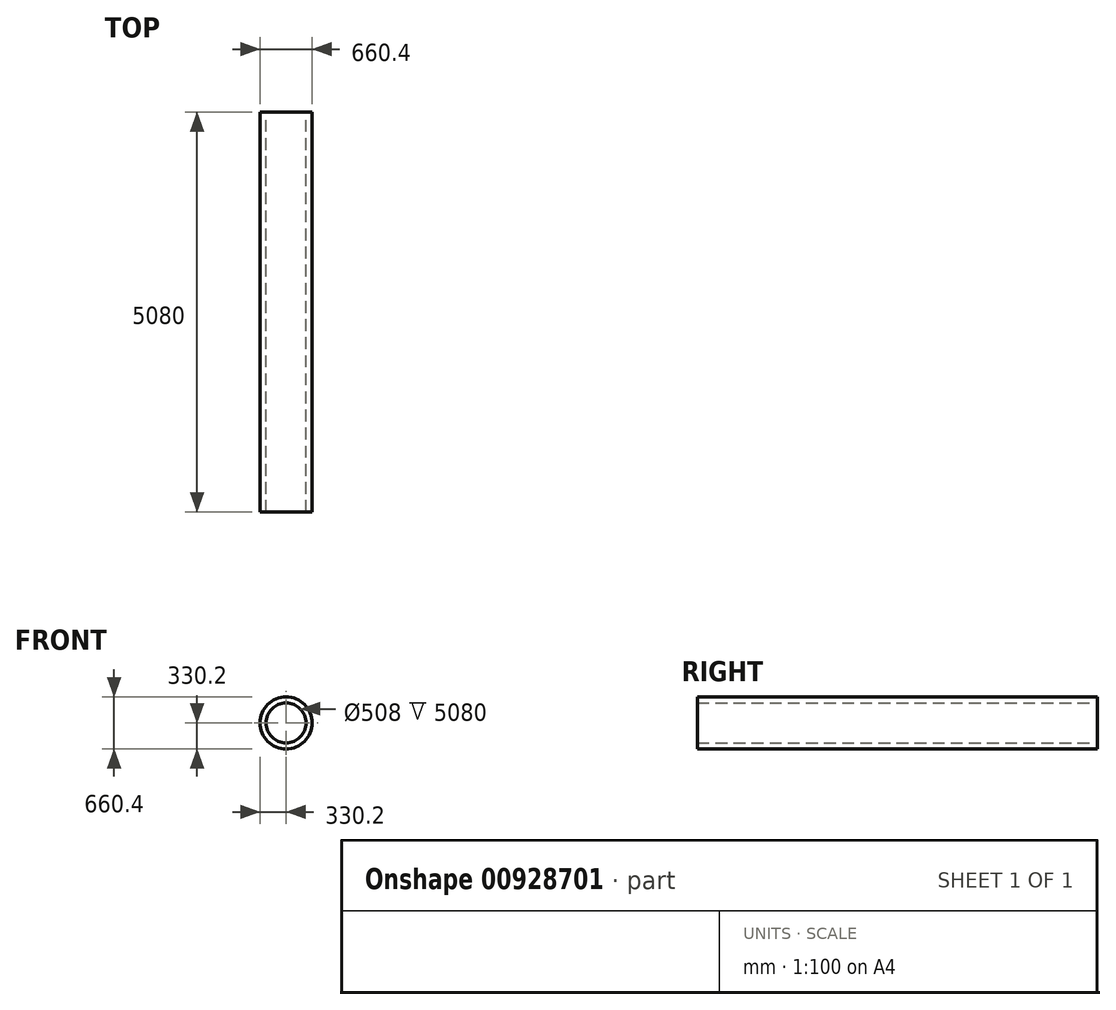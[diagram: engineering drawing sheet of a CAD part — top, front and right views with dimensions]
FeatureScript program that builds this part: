
annotation { "Feature Type Name" : "Feature", "Feature Type Description" : "" }
export const myFeature = defineFeature(function(context is Context, id is Id, definition is map)
    precondition{}
    {
        {
            var Q0;
            Q0=qCreatedBy(makeId("Front.planeOp"),FACE);
            var sketch = newSketch(context, id + "F0", { "sketchPlane" : qUnion([Q0])});
            skCircle(sketch, "E0", {"center": v(0, 0) * mm, "radius": 254 * mm});
            skCircle(sketch, "E1", {"center": v(0, 0) * mm, "radius": 330.2 * mm});
            skSolve(sketch);
        }
        {
            var Q0;
            Q0=makeQuery(id+"F0.imprint","IMPRINT",FACE,{"disambiguationData":[TD([[makeQuery(id+"F0.imprint","IMPRINT",EDGE,{"derivedFrom":sQuery(id+"F0.wireOp",EDGE,"E0")}),-1.0]])]});
            extrude(context, id + "F1", {"entities" : qUnion([Q0]), "depth" : 5080 * mm, "offsetDistance" : 25.4 * mm});
        }
    });
